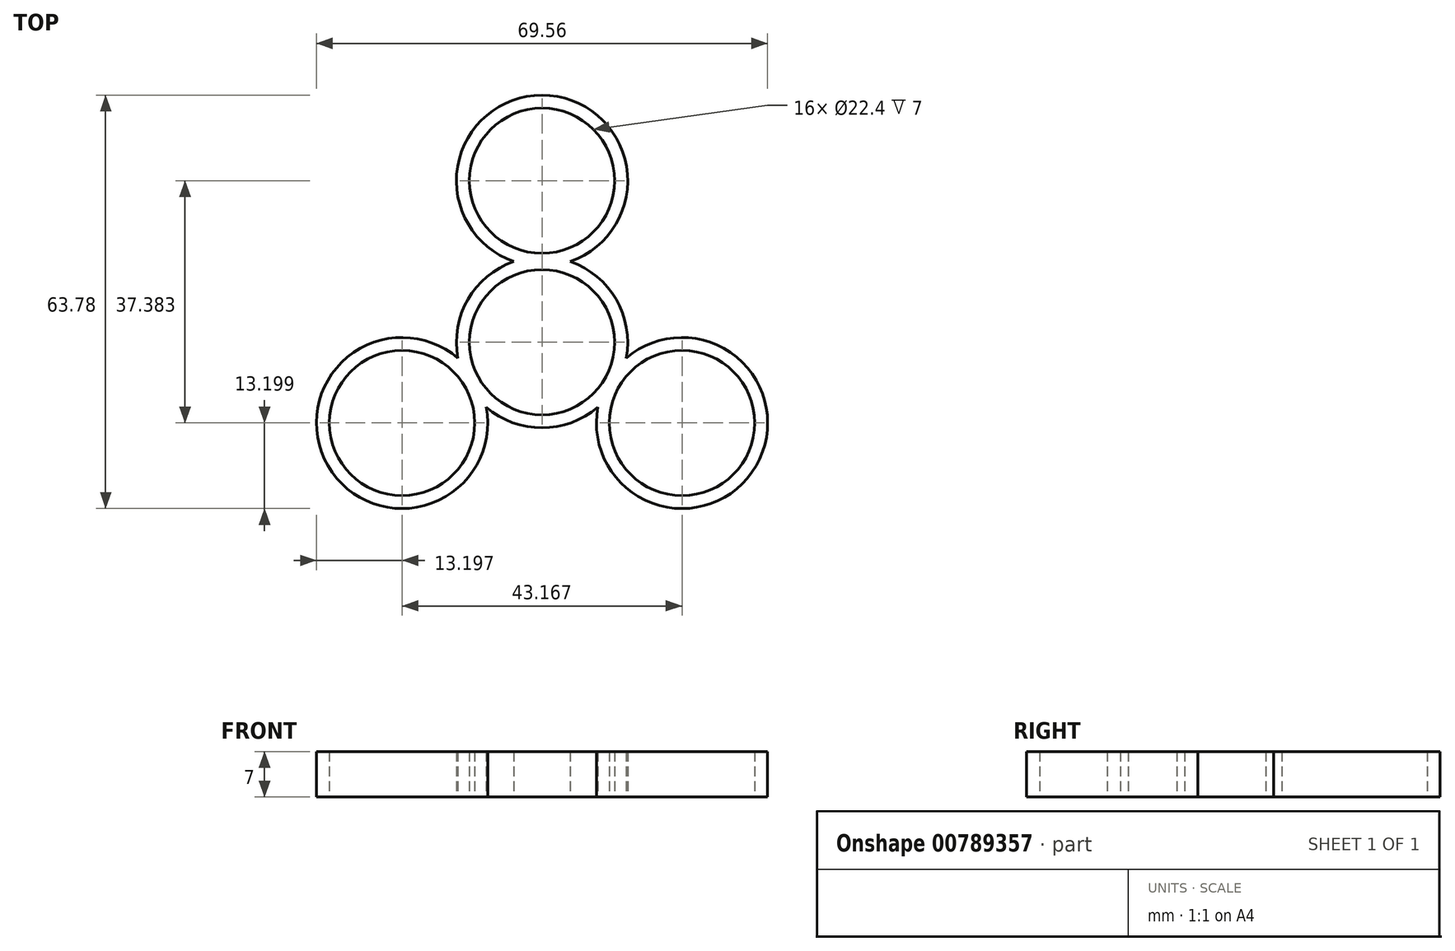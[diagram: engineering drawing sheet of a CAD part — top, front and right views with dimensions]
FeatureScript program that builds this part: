
annotation { "Feature Type Name" : "Feature", "Feature Type Description" : "" }
export const myFeature = defineFeature(function(context is Context, id is Id, definition is map)
    precondition{}
    {
        {
            var Q0;
            Q0=qCreatedBy(makeId("Top.planeOp"),FACE);
            var sketch = newSketch(context, id + "F0", { "sketchPlane" : qUnion([Q0])});
            skCircle(sketch, "E0", {"center": v(0, 0) * mm, "radius": 11.2 * mm});
            skCircle(sketch, "E1", {"center": v(0, 0) * mm, "radius": 13.2 * mm});
            skCircle(sketch, "E2", {"center": v(0, 24.92) * mm, "radius": 13.2 * mm});
            skCircle(sketch, "E3", {"center": v(0, 24.92) * mm, "radius": 11.2 * mm});
            skCircle(sketch, "E4.1.0", {"center": v(-21.58, -12.46) * mm, "radius": 13.2 * mm});
            skCircle(sketch, "E4.1.1", {"center": v(-21.58, -12.46) * mm, "radius": 11.2 * mm});
            skCircle(sketch, "E4.2.0", {"center": v(21.58, -12.46) * mm, "radius": 13.2 * mm});
            skCircle(sketch, "E4.2.1", {"center": v(21.58, -12.46) * mm, "radius": 11.2 * mm});
            skSolve(sketch);
        }
        {
            var Q0;
            Q0 = qSketchRegion(id + "F0", true);
            extrude(context, id + "F1", {"entities" : qUnion([Q0]), "depth" : 7 * mm, "offsetDistance" : 25 * mm});
        }
    });
